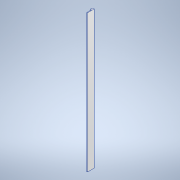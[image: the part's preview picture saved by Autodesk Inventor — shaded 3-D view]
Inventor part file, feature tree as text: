
AUTODESK INVENTOR PART (.ipt)
format: ipt  version: 2022 (Build 260153000, 153)  size: 100,352 bytes
history: native  units: mm
features: sketch x2, extrude x1
ambient origin geometry x8: Origin, YZ Plane, XZ Plane, XY Plane, X Axis, Y Axis, Z Axis, Center Point
bodies: Solid1 (feature_tree)
feature tree (3):
  sketch  "Sketch1"  dims[d0=44.0mm d1=6.0mm]
  extrude  "Extrusion1"  Depth=6.0mm
  sketch  "Sketch2"  dims[d2=10.0mm d3=65.0mm d4=1300.0mm d5=0.0mm]
